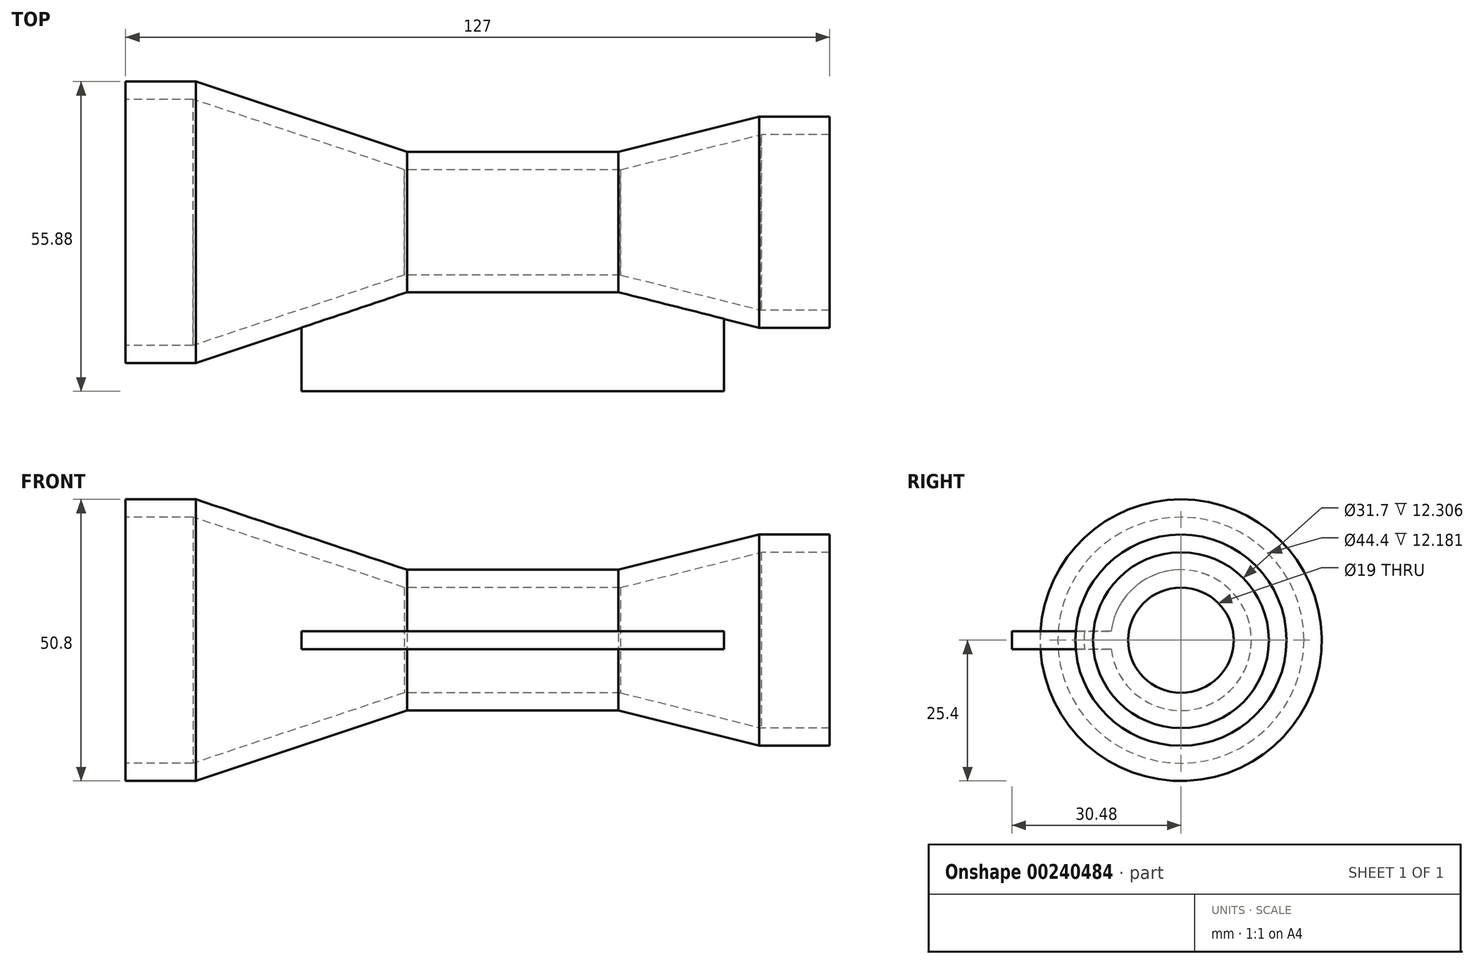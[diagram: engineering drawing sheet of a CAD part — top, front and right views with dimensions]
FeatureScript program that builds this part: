
annotation { "Feature Type Name" : "Feature", "Feature Type Description" : "" }
export const myFeature = defineFeature(function(context is Context, id is Id, definition is map)
    precondition{}
    {
        {
            var Q0;
            Q0=qCreatedBy(makeId("Top.planeOp"),FACE);
            var sketch = newSketch(context, id + "F0", { "sketchPlane" : qUnion([Q0])});
            skLineSegment(sketch, "E0", {"start": v(-69.85, 0) * mm, "end": v(57.15, 0) * mm, "construction": true});
            skLineSegment(sketch, "E1", {"start": v(57.15, 15.85) * mm, "end": v(57.15, 19.05) * mm});
            skLineSegment(sketch, "E2", {"start": v(57.15, 19.05) * mm, "end": v(44.45, 19.05) * mm});
            skLineSegment(sketch, "E3", {"start": v(44.45, 19.05) * mm, "end": v(19.05, 12.7) * mm});
            skLineSegment(sketch, "E4", {"start": v(19.05, 12.7) * mm, "end": v(-19.05, 12.7) * mm});
            skLineSegment(sketch, "E5", {"start": v(-19.05, 12.7) * mm, "end": v(-57.15, 25.4) * mm});
            skLineSegment(sketch, "E6", {"start": v(-57.15, 25.4) * mm, "end": v(-69.85, 25.4) * mm});
            skLineSegment(sketch, "E7", {"start": v(-69.85, 25.4) * mm, "end": v(-69.85, 22.2) * mm});
            skLineSegment(sketch, "E8.0", {"start": v(-57.67, 22.2) * mm, "end": v(-69.85, 22.2) * mm});
            skLineSegment(sketch, "E8.1", {"start": v(57.15, 15.85) * mm, "end": v(44.84, 15.85) * mm});
            skLineSegment(sketch, "E8.2", {"start": v(44.84, 15.85) * mm, "end": v(19.44, 9.5) * mm});
            skLineSegment(sketch, "E8.3", {"start": v(19.44, 9.5) * mm, "end": v(-19.57, 9.5) * mm});
            skLineSegment(sketch, "E8.4", {"start": v(-19.57, 9.5) * mm, "end": v(-57.67, 22.2) * mm});
            skPoint(sketch, "E9", {"position": v(0, 12.7) * mm});
            skSolve(sketch);
        }
        {
            var Q0;
            Q0 = qSketchRegion(id + "F0", true);
            var Q1;
            Q1=sQuery(id+"F0.wireOp",EDGE,"E0");
            revolve(context, id + "F1", {"entities" : qUnion([Q0]), "axis" : qUnion([Q1]), "revolveType" : RevolveType.FULL});
        }
        {
            var Q0;
            Q0=qCreatedBy(makeId("Front.planeOp"),FACE);
            cPlane(context, id + "F2", {"entities" : qUnion([Q0]), "cplaneType" : CPlaneType.OFFSET, "offset" : 30.48 * mm, "width" : 152.4 * mm, "height" : 152.4 * mm});
        }
        {
            var Q0;
            Q0=qCreatedBy(id+"F2.planeOp",FACE);
            var sketch = newSketch(context, id + "F3", { "sketchPlane" : qUnion([Q0])});
            skLineSegment(sketch, "E10.bottom", {"start": v(-38.1, 1.6) * mm, "end": v(38.1, 1.6) * mm});
            skLineSegment(sketch, "E10.top", {"start": v(-38.1, -1.6) * mm, "end": v(38.1, -1.6) * mm});
            skLineSegment(sketch, "E10.left", {"start": v(-38.1, 1.6) * mm, "end": v(-38.1, -1.6) * mm});
            skLineSegment(sketch, "E10.right", {"start": v(38.1, 1.6) * mm, "end": v(38.1, -1.6) * mm});
            skLineSegment(sketch, "E11", {"start": v(0, 28.1) * mm, "end": v(0, -30.04) * mm, "construction": true});
            skPoint(sketch, "E12", {"position": v(38.1, 0) * mm});
            skPoint(sketch, "E13", {"position": v(0, 1.6) * mm});
            skSolve(sketch);
        }
        {
            var Q0;
            Q0 = qSketchRegion(id + "F3", true);
            extrude(context, id + "F4", {"entities" : qUnion([Q0]), "operationType" : NewBodyOperationType.ADD, "endBound" : BoundingType.UP_TO_NEXT, "oppositeDirection" : true, "depth" : 25.4 * mm});
        }
    });
